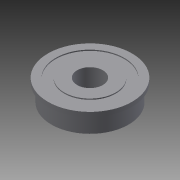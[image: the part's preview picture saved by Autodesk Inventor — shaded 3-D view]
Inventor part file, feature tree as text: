
AUTODESK INVENTOR PART (.ipt)
format: ipt  version: 2014 SP1 (Build 180222100, 222)  size: 117,248 bytes
history: native  units: in
note: dims shown in document units (in); Inventor stores cm internally (conversion verified against a paired STEP export)
features: revolve x1, imported_body x1
ambient origin geometry x8: Origin, YZ Plane, XZ Plane, XY Plane, X Axis, Y Axis, Z Axis, Center Point
bodies: Body1 (feature_tree)
feature tree (2):
  revolve  "Revolve1"  [1 undecoded]
  imported_body  "Base1"
note: 1 required parameter value undecoded (feature->parameter linkage not recoverable at this tier; creation-order binding heuristic only, values carry confidence <= 0.55)
